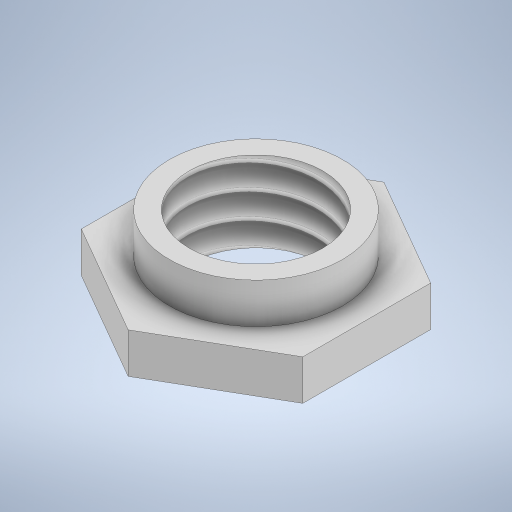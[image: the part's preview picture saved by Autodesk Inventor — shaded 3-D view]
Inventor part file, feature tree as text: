
AUTODESK INVENTOR PART (.ipt)
format: ipt  version: 2023 (Build 270158030, 158C)  size: 266,240 bytes
history: native  units: mm
features: sketch x3, extrude x2, hole x1
ambient origin geometry x8: Origin, YZ Plane, XZ Plane, XY Plane, X Axis, Y Axis, Z Axis, Center Point
bodies: Solid1 (feature_tree)
feature tree (6):
  extrude  "Extrusion1"  Depth=2.0mm TaperAngle=0.0deg
  extrude  "Extrusion2"  Depth=2.0mm TaperAngle=0.0deg
  hole  "Hole1"  [1 undecoded]
  sketch  "Sketch1"  dims[d0=11.0mm d1=2.0mm d2=0.0mm]
  sketch  "Sketch2"  dims[d3=8.6mm d4=2.0mm d5=0.0mm]
  sketch  "Sketch3"  dims[d6=8.0mm d7=6.647mm d8=16.0mm d9=4.0mm d10=2.0mm d11=90.0deg d12=8.0mm d13=0.0mm]
note: 1 required parameter value undecoded (feature->parameter linkage not recoverable at this tier; creation-order binding heuristic only, values carry confidence <= 0.55)
